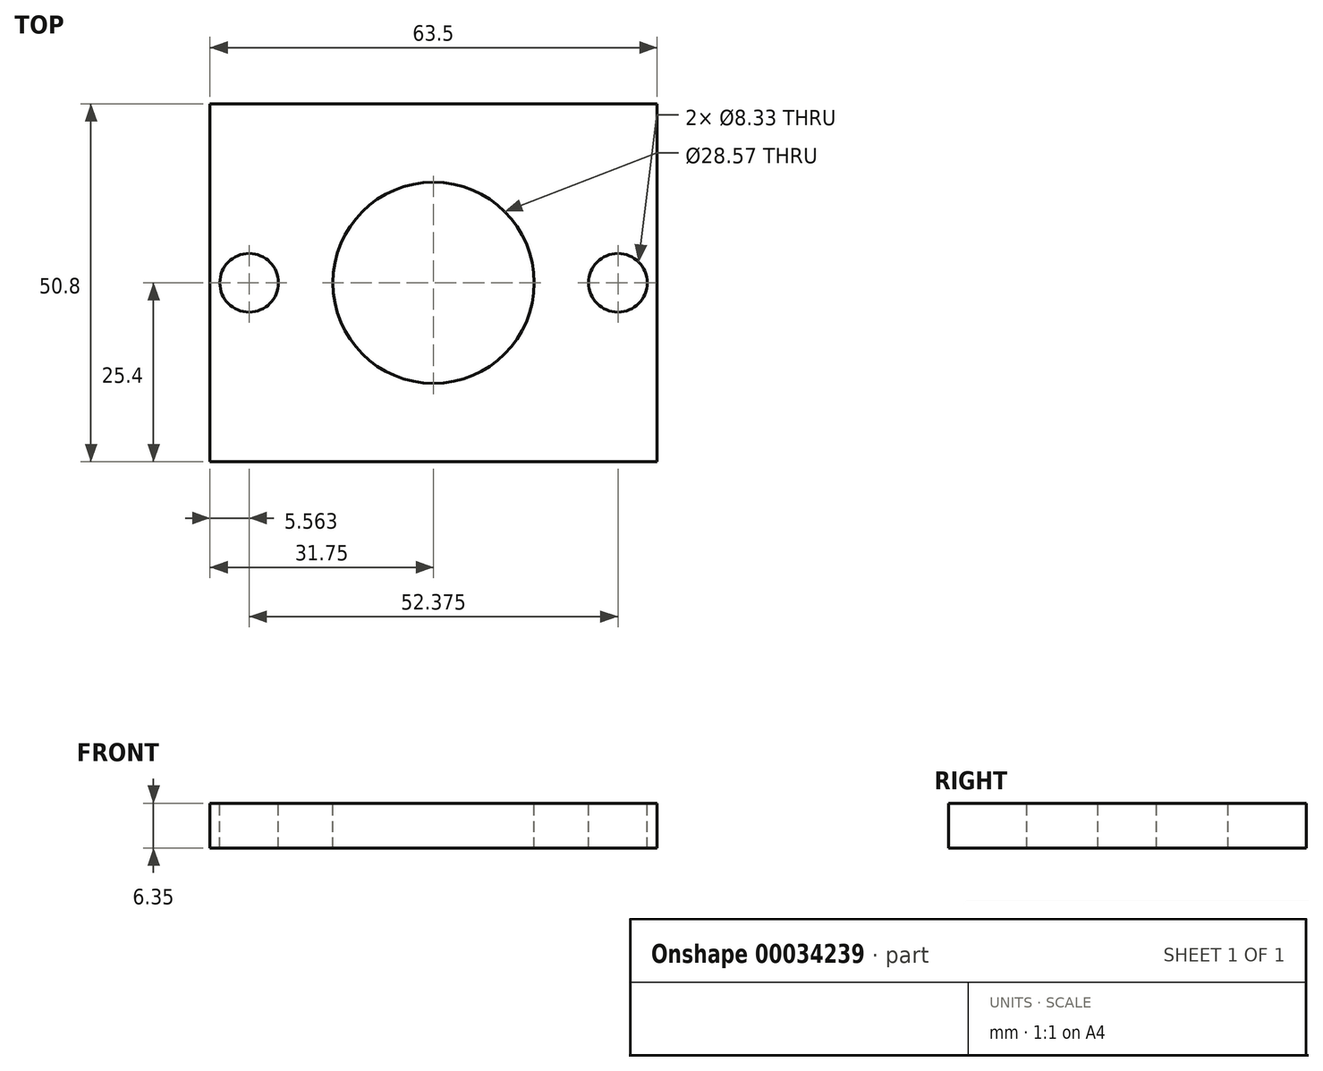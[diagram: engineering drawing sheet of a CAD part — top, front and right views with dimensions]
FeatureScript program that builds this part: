
annotation { "Feature Type Name" : "Feature", "Feature Type Description" : "" }
export const myFeature = defineFeature(function(context is Context, id is Id, definition is map)
    precondition{}
    {
        {
            var Q0;
            Q0=qCreatedBy(makeId("Top.planeOp"),FACE);
            var sketch = newSketch(context, id + "F0", { "sketchPlane" : qUnion([Q0])});
            skCircle(sketch, "E0", {"center": v(0, 0) * mm, "radius": 14.29 * mm});
            skLineSegment(sketch, "E1.bottom", {"start": v(-31.75, 25.4) * mm, "end": v(31.75, 25.4) * mm});
            skLineSegment(sketch, "E1.top", {"start": v(-31.75, -25.4) * mm, "end": v(31.75, -25.4) * mm});
            skLineSegment(sketch, "E1.left", {"start": v(-31.75, 25.4) * mm, "end": v(-31.75, -25.4) * mm});
            skLineSegment(sketch, "E1.right", {"start": v(31.75, 25.4) * mm, "end": v(31.75, -25.4) * mm});
            skCircle(sketch, "E2", {"center": v(-26.19, 0) * mm, "radius": 4.17 * mm});
            skCircle(sketch, "E3", {"center": v(26.19, 0) * mm, "radius": 4.17 * mm});
            skSolve(sketch);
        }
        {
            var Q0;
            Q0=makeQuery(id+"F0.imprint","IMPRINT",FACE,{"disambiguationData":[TD([[makeQuery(id+"F0.imprint","IMPRINT",EDGE,{"derivedFrom":sQuery(id+"F0.wireOp",EDGE,"E0")}),-1.0]])]});
            extrude(context, id + "F1", {"entities" : qUnion([Q0]), "oppositeDirection" : true, "depth" : 6.35 * mm});
        }
    });
